# Revit family: Pablo-IP_65-Transparent_Door-syst-IT-en
name_source: partatom
category: Electrical Equipment
units: mm (PartAtom-declared; Revit-internal decimal feet)

## family parameters
Cut with Voids When Loaded = No
Host = Face
Panel Configuration = Two Columns, Circuits Across
Part Type = Panelboard
Room Calculation Point = No
Round Connector Dimension = Use Diameter
Shared = No

## types (8) — shared parameters
EF000003 - Mounting method = EV000384 - Surface mounted (plaster)
EF000007 - Colour = EV000270 - Grey
EF000116 - RAL-number = 7035
EF000118 - With mounting plate = No
EF000339 - Type of cover = EV004216 - Door
EF001062 - EMC-version = No
EF001088 - Extension possible = No
EF001134 - DIN-rail = Yes
EF001596 - Material housing = EV000139 - Plastic
EF004462 - Type of closure = EV000154 - Other
EF005474 - Degree of protection (IP) = EV006421 - IP65
EF006244 - Transparent cover/door = Yes
EF006306 - With lock = No
EF009212 - Cover model = EV000116 - Closed
EF015776 - Earthing terminal block = No
EF015777 - Neutral terminal block = No
EF015941 - Signal passing door = No
HG000001 - Number of columns = 1
HG000002 - With door or cover = Yes
HG000003 - Range = Pablo
HG000005 - Thickness = 3 mm  [stored 0.00984252 ft]
HG000006 - Flush mounted = No
HG000009 - Double swing door = No
HG000010 - Asymmetric doors = No
HG000011 - Empty rows from bottom = No
Manufacturer = Hager
Type Comments = Pablo
zero-valued in all types: Default Elevation, EF000218 - Built-in depth, EF000332 - Built-in height, EF000846 - Built-in width, HG000007 - Number of empty columns, HG000008 - Number of empty rows

## per-type parameters (varying)
| type | EF000008 - Width | EF000040 - Height | EF000049 - Depth | EF000266 - Number of rows | EF001131 - Internal depth | EF002950 - Width in number of modular spacings | HG000004 - Manufacturer reference | Model |
| Surface mounted IP65 W143 H210 D102 4 Modular spacings - B06521 | 143 mm | 210 mm | 102 mm | 1 | 102 mm | 4 | B06521 | B06521 |
| Surface mounted IP65 W215 H210 D105 8 Modular spacings - B06522 | 215 mm | 210 mm | 105 mm | 1 | 105 mm | 8 | B06522 | B06522 |
| Surface mounted IP65 W314 H263 D143 12 Modular spacings - B06523 | 314 mm | 263 mm | 143 mm | 1 | 143 mm | 12 | B06523 | B06523 |
| Surface mounted IP65 W314 H420 D143 12 Modular spacings - B06525 | 314 mm | 420 mm  [stored 1.37795 ft] | 143 mm | 2 | 143 mm | 12 | B06525 | B06525 |
| Surface mounted IP65 W426 H288 D148 18 Modular spacings - B06524 | 426 mm  [stored 1.39764 ft] | 288 mm | 148 mm | 1 | 148 mm | 18 | B06524 | B06524 |
| Surface mounted IP65 W426 H470 D148 19 Modular spacings - B06526 | 426 mm  [stored 1.39764 ft] | 470 mm | 148 mm | 2 | 148 mm | 19 | B06526 | B06526 |
| Surface mounted IP65 W426 H657 D148 19 Modular spacings - B06527 | 426 mm  [stored 1.39764 ft] | 657 mm | 148 mm | 3 | 148 mm | 19 | B06527 | B06527 |
| Surface mounted IP65 W426 H903 D168 19 Modular spacings - B06528 | 426 mm  [stored 1.39764 ft] | 903 mm  [stored 2.9626 ft] | 168 mm  [stored 0.551181 ft] | 4 | 168 mm  [stored 0.551181 ft] | 19 | B06528 | B06528 |

note: [stored X ft] marks values corroborated as IEEE doubles in the binary element streams (Revit-internal decimal feet)

## geometry (parser evidence)
native form markers: Sweep x12
no freeform markers — native parametric forms only
